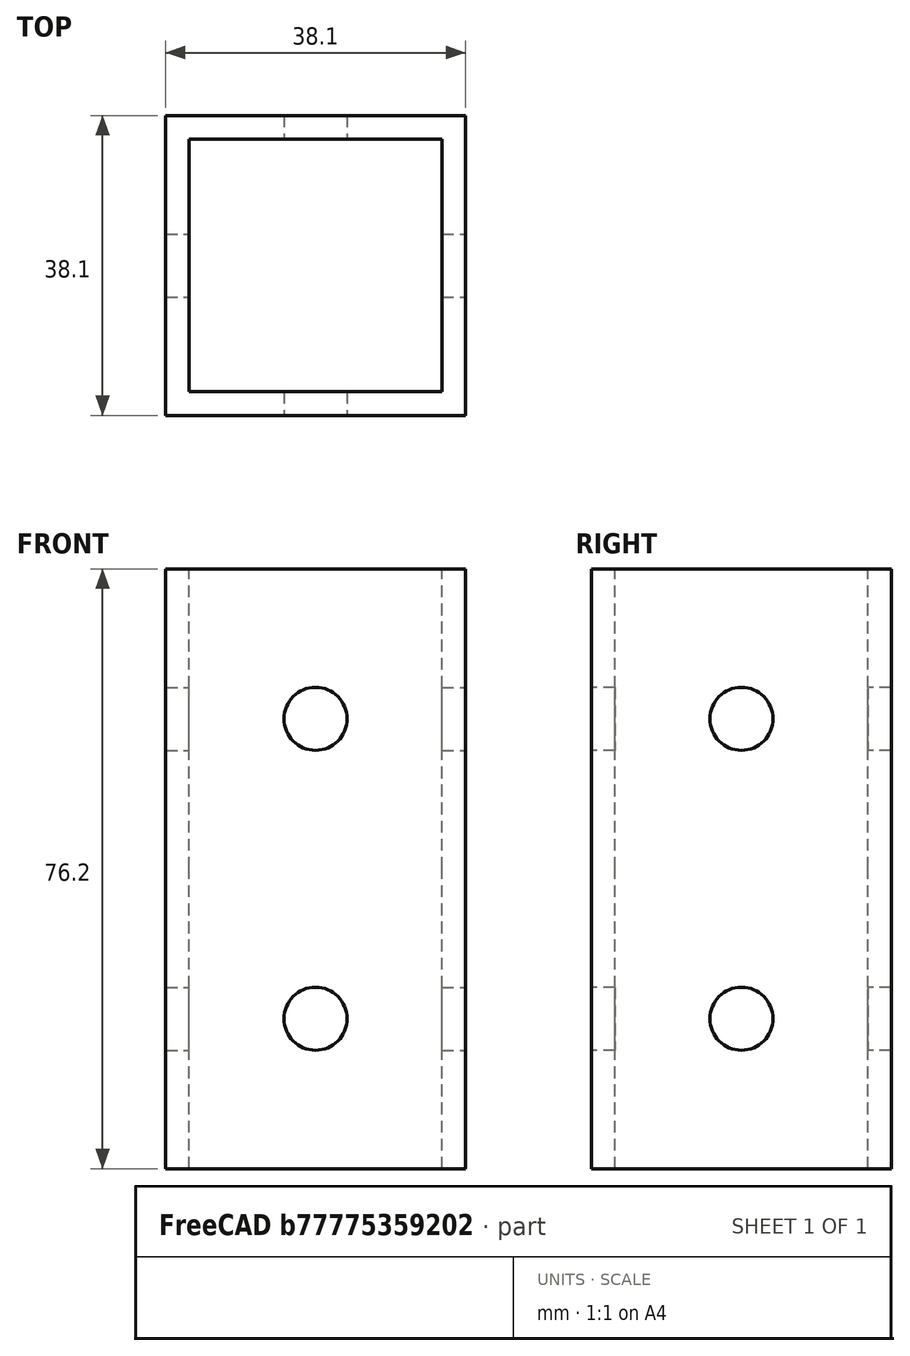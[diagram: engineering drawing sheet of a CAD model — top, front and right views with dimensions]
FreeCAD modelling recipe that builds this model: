
FCSTD DOCUMENT  (FreeCAD 0.15R4671 (Git))
Label: 2x-fillet-hollow
License: All rights reserved
LicenseURL: http://en.wikipedia.org/wiki/All_rights_reserved
objects: Part::Cut×6, Part::Box×4, Part::Cylinder×4, PartDesign::Fillet×2, Part::MultiFuse×1
note: 17 computed .brp shape members not serialized (recipe doc carries the construction recipe); baked Part::Feature solids carry a one-line shape summary decoded from their .brp

FEATURE [Part::Box] Box  label="Cube"
  Height = 38.1
  Length = 38.1
  Width = 38.1
FEATURE [Part::Cylinder] Cylinder
  Angle = 360
  Height = 38.1
  Placement = pos=(19.05,38.1,19.05) rot=(1,0,0;1.5708rad)
  Radius = 4
FEATURE [Part::Cylinder] Cylinder001
  Angle = 360
  Height = 38.1
  Placement = pos=(0,19.05,19.05) rot=(0,1,0;1.5708rad)
  Radius = 4
FEATURE [Part::Cut] Cut
  Base = -> Box
  Tool = -> Cylinder
FEATURE [Part::Cut] Cut001
  Base = -> Cut
  Tool = -> Cylinder001
FEATURE [Part::Box] Box001  label="Cube001"
  Height = 38.1
  Length = 32.1
  Placement = pos=(3,3,0) rot=(0,0,1;0rad)
  Width = 32.1
FEATURE [Part::Cut] Cut002
  Base = -> Cut001
  Tool = -> Box001
FEATURE [PartDesign::Fillet] Fillet
  Base = -> Cut002 [Edge4,Edge1,Edge22,Edge7]
  Radius = 1
FEATURE [Part::Box] Box002  label="Cube002"
  Height = 38.1
  Length = 38.1
  Width = 38.1
FEATURE [Part::Cylinder] Cylinder002
  Angle = 360
  Height = 38.1
  Placement = pos=(19.05,38.1,19.05) rot=(1,0,0;1.5708rad)
  Radius = 4
FEATURE [Part::Cylinder] Cylinder003
  Angle = 360
  Height = 38.1
  Placement = pos=(0,19.05,19.05) rot=(0,1,0;1.5708rad)
  Radius = 4
FEATURE [Part::Cut] Cut003
  Base = -> Box002
  Tool = -> Cylinder002
FEATURE [Part::Cut] Cut004
  Base = -> Cut003
  Tool = -> Cylinder003
FEATURE [Part::Box] Box003  label="Cube003"
  Height = 38.1
  Length = 32.1
  Placement = pos=(3,3,0) rot=(0,0,1;0rad)
  Width = 32.1
FEATURE [Part::Cut] Cut005
  Base = -> Cut004
  Placement = pos=(0,0,38.1) rot=(0,0,1;0rad)
  Tool = -> Box003
FEATURE [PartDesign::Fillet] Fillet001
  Base = -> Cut005 [Edge4,Edge1,Edge22,Edge7]
  Placement = pos=(0,0,38.1) rot=(0,0,1;0rad)
  Radius = 1
FEATURE [Part::MultiFuse] Fusion
  Shapes = -> [Cut002,Fillet,Cut005,Fillet001]
